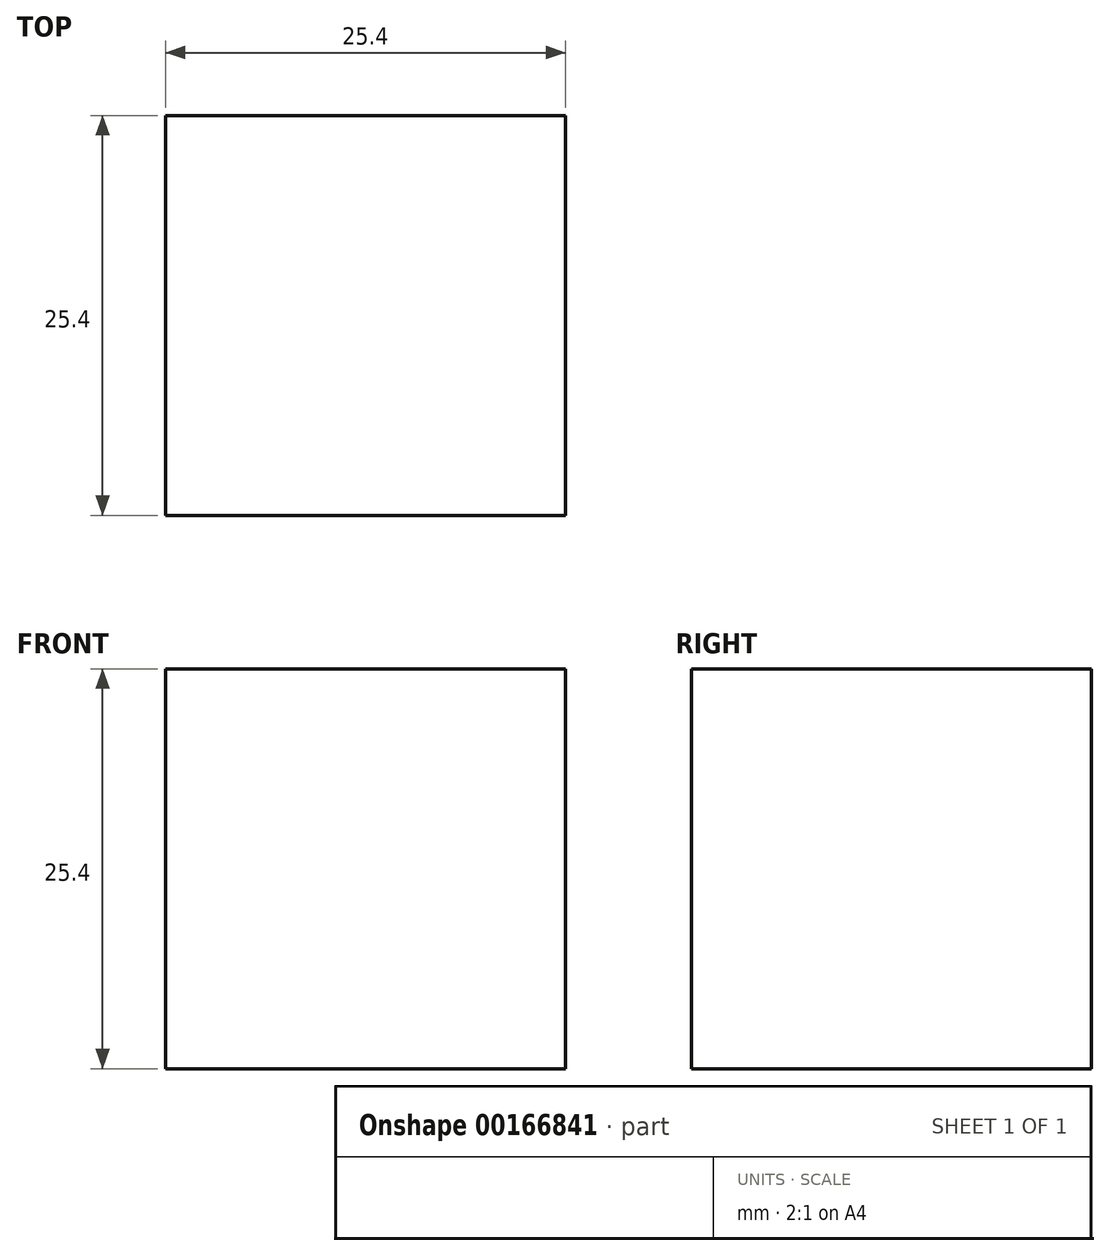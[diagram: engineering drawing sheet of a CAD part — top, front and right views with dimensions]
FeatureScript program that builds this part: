
annotation { "Feature Type Name" : "Feature", "Feature Type Description" : "" }
export const myFeature = defineFeature(function(context is Context, id is Id, definition is map)
    precondition{}
    {
        {
            var Q0;
            Q0=qCreatedBy(makeId("Top.planeOp"),FACE);
            var sketch = newSketch(context, id + "F0", { "sketchPlane" : qUnion([Q0])});
            skLineSegment(sketch, "E0.bottom", {"start": v(12.7, -12.7) * mm, "end": v(-12.7, -12.7) * mm});
            skLineSegment(sketch, "E0.top", {"start": v(12.7, 12.7) * mm, "end": v(-12.7, 12.7) * mm});
            skLineSegment(sketch, "E0.left", {"start": v(12.7, -12.7) * mm, "end": v(12.7, 12.7) * mm});
            skLineSegment(sketch, "E0.right", {"start": v(-12.7, -12.7) * mm, "end": v(-12.7, 12.7) * mm});
            skPoint(sketch, "E0.middle", {"position": v(0, 0) * mm});
            skSolve(sketch);
        }
        {
            var Q0;
            Q0=makeQuery(id+"F0.imprint","IMPRINT",FACE,{"disambiguationData":[TD([[makeQuery(id+"F0.imprint","IMPRINT",EDGE,{"derivedFrom":sQuery(id+"F0.wireOp",EDGE,"E0.bottom")}),-1.0]])]});
            extrude(context, id + "F1", {"entities" : qUnion([Q0]), "depth" : 25.4 * mm});
        }
    });
